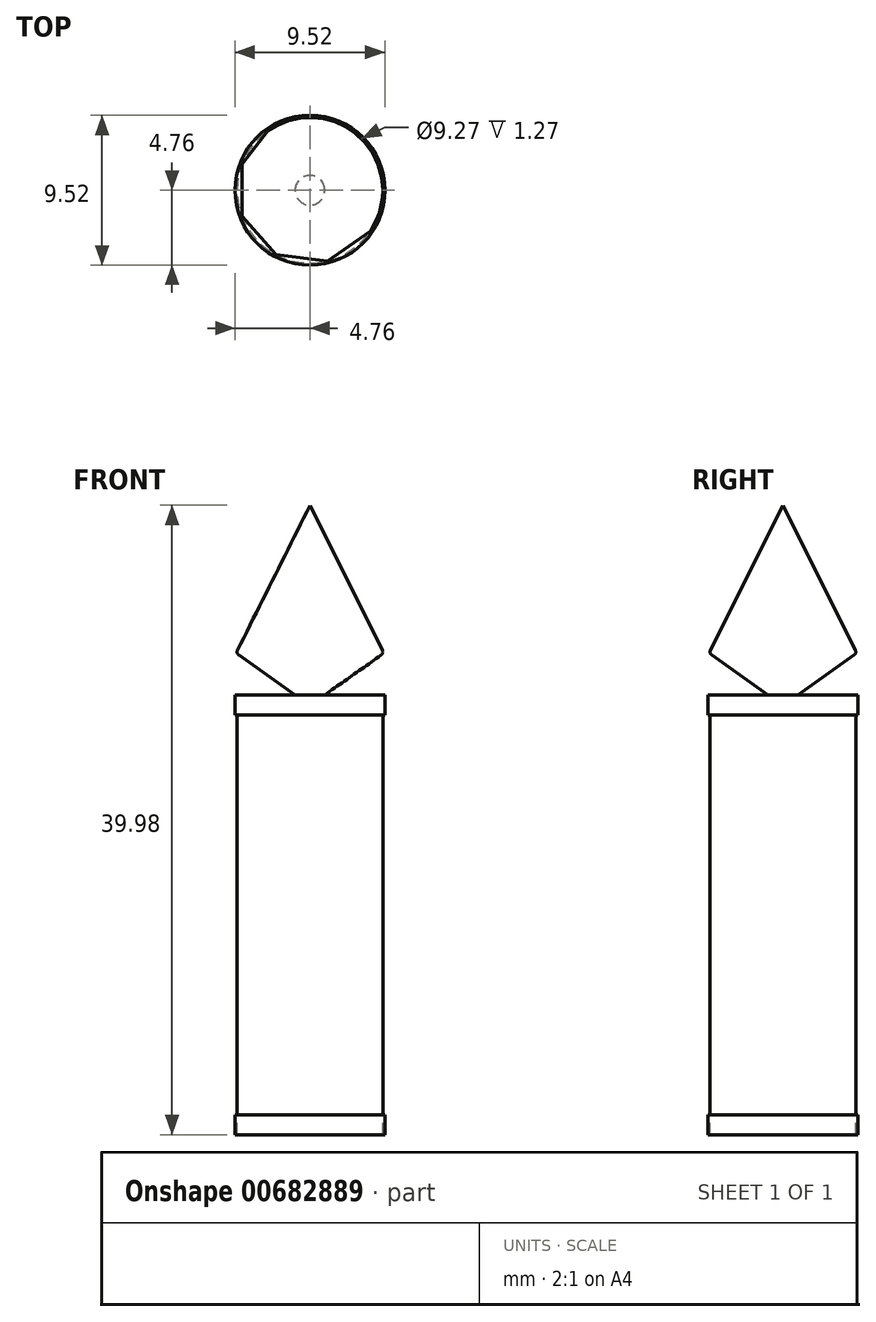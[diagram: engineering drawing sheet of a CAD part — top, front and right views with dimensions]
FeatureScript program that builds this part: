
annotation { "Feature Type Name" : "Feature", "Feature Type Description" : "" }
export const myFeature = defineFeature(function(context is Context, id is Id, definition is map)
    precondition{}
    {
        {
            var Q0;
            Q0=qCreatedBy(makeId("Top.planeOp"),FACE);
            var sketch = newSketch(context, id + "F0", { "sketchPlane" : qUnion([Q0])});
            skCircle(sketch, "E0", {"center": v(0, 0) * mm, "radius": 4.64 * mm});
            skSolve(sketch);
        }
        {
            var Q0;
            Q0 = qSketchRegion(id + "F0", true);
            extrude(context, id + "F1", {"entities" : qUnion([Q0]), "depth" : 25.4 * mm, "offsetDistance" : 25.4 * mm});
        }
        {
            var Q0;
            Q0=makeQuery(id+"F1.opExtrude","CAP_FACE",FACE,{"disambiguationData":[OSD([sQuery(id+"F0.wireOp",EDGE,"E0")])],"isStart":false});
            var sketch = newSketch(context, id + "F2", { "sketchPlane" : qUnion([Q0])});
            skCircle(sketch, "E1", {"center": v(0, 0) * mm, "radius": 4.76 * mm});
            skSolve(sketch);
        }
        {
            var Q0;
            Q0 = qSketchRegion(id + "F2", true);
            extrude(context, id + "F3", {"entities" : qUnion([Q0]), "operationType" : NewBodyOperationType.ADD, "depth" : 1.27 * mm, "offsetDistance" : 25.4 * mm});
        }
        {
            var Q0;
            Q0=makeQuery(id+"F1.opExtrude","CAP_FACE",FACE,{"disambiguationData":[OSD([sQuery(id+"F0.wireOp",EDGE,"E0")])],"isStart":true});
            var sketch = newSketch(context, id + "F4", { "sketchPlane" : qUnion([Q0])});
            skCircle(sketch, "E2", {"center": v(0, 0) * mm, "radius": 4.76 * mm});
            skSolve(sketch);
        }
        {
            var Q0;
            Q0=makeQuery(id+"F4.imprint","IMPRINT",FACE,{"disambiguationData":[TD([[makeQuery(id+"F4.imprint","IMPRINT",EDGE,{"derivedFrom":sQuery(id+"F4.wireOp",EDGE,"E2")}),1.0]])]});
            extrude(context, id + "F5", {"entities" : qUnion([Q0]), "depth" : 1.27 * mm, "offsetDistance" : 25.4 * mm});
        }
        {
            var Q0;
            Q0=qCreatedBy(makeId("Right.planeOp"),FACE);
            var sketch = newSketch(context, id + "F6", { "sketchPlane" : qUnion([Q0])});
            skLineSegment(sketch, "E3", {"start": v(0, 26) * mm, "end": v(0, 38.7) * mm});
            skLineSegment(sketch, "E4", {"start": v(4.7, 29.31) * mm, "end": v(0, 38.7) * mm});
            skLineSegment(sketch, "E5", {"start": v(4.7, 29.31) * mm, "end": v(0, 26) * mm});
            skSolve(sketch);
        }
        {
            var Q0;
            Q0=makeQuery(id+"F6.imprint","IMPRINT",FACE,{"disambiguationData":[TD([[makeQuery(id+"F6.imprint","IMPRINT",EDGE,{"derivedFrom":sQuery(id+"F6.wireOp",EDGE,"E3")}),-1.0]])]});
            var Q1;
            Q1=sQuery(id+"F6.wireOp",EDGE,"E3");
            revolve(context, id + "F7", {"operationType" : NewBodyOperationType.ADD, "surfaceOperationType" : NewSurfaceOperationType.NEW, "entities" : qUnion([Q0]), "axis" : qUnion([Q1]), "revolveType" : RevolveType.FULL});
        }
        {
            var Q0;
            Q0=makeQuery(id+"F7.opRevolve","SWEPT_FACE",FACE,{"disambiguationData":[OSD([sQuery(id+"F6.wireOp",EDGE,"E4")])]});
            fillet(context, id + "F8", {"entities" : qUnion([Q0]), "radius" : 0.25 * mm, "tangentPropagation" : true, "allowEdgeOverflow" : false});
        }
    });
